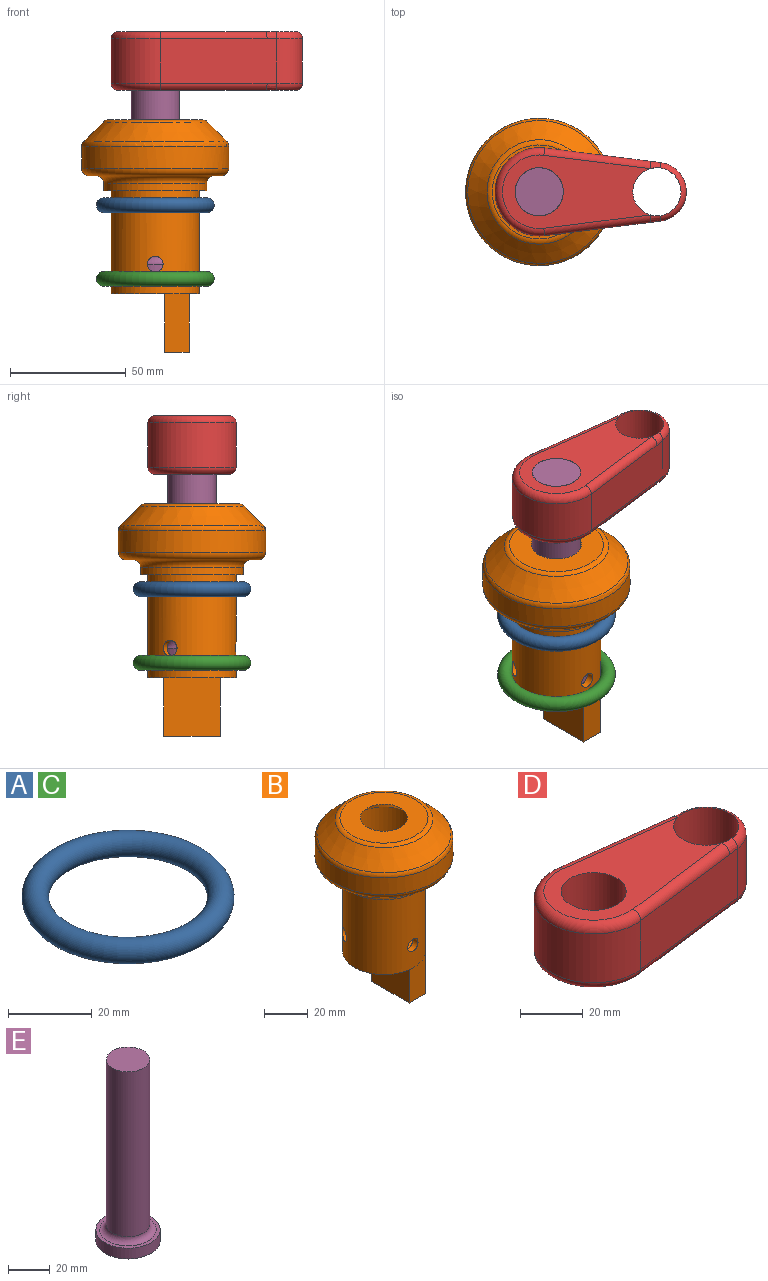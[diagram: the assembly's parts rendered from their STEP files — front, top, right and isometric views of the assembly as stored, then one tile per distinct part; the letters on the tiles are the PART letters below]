
ASSEMBLY  parts=5 mates=4
PART A: 1 faces, bbox 55x55x6.4 mm
  f0: torus R=22.23mm, axis (0,0,1), area 2785.8mm2
PART B: 24 faces, bbox 68.7x68.7x100.3 mm
  f0: plane 38.1x33.64mm, normal (0,0,-1), area 810.7mm2, adj f2,f19,f21,f22
  f1: plane 24.49x4.46mm, normal (0,0,-1), area 74.7mm2, adj f2,f20
  f2: cylinder r=19.05mm len=44.45mm, axis (0,0,-1), area 5212.8mm2, adj f0,f1,f5,f12,f13,f14
  f3: cylinder r=15.88mm len=63.5mm, axis (0,0,-1), area 6226mm2, adj f4,f11,f12,f13,f14
  f4: plane 31.75x31.75mm, normal (0,0,1), area 791.7mm2, adj f3
  f5: plane 44.45x44.45mm, normal (0,0,-1), area 411.7mm2, adj f2,f6
  f6: cylinder r=22.23mm len=44.45mm, axis (0,0,-1), area 443.4mm2, adj f5,f15
  f7: plane 57.15x57.15mm, normal (0,0,-1), area 538.4mm2, adj f15,f16
  f8: cylinder r=31.75mm len=63.5mm, axis (0,0,-1), area 1891.2mm2, adj f16,f17
  f9: cone r=31.75mm half-angle=45deg, axis (0,0,-1), area 1967mm2, adj f17,f18
  f10: plane 40.55x40.55mm, normal (0,0,1), area 925.3mm2, adj f11,f18
  f11: cone r=15.88mm half-angle=45deg, axis (0,0,-1), area 601.9mm2, adj f3,f10
  f12: cylinder r=3.38mm len=6.76mm, axis (0,1,0), area 68mm2, adj f2,f3
  f13: cylinder r=3.38mm len=7.62mm, axis (0.87,-0.5,0), area 68mm2, adj f2,f3
  f14: cylinder r=3.38mm len=7.62mm, axis (-0.87,-0.5,0), area 68mm2, adj f2,f3
  f15: torus R=25.4mm, axis (0,0,-1), area 732.6mm2, adj f6,f7
  f16: torus R=28.57mm, axis (0,0,-1), area 958.8mm2, adj f7,f8
  f17: torus R=28.57mm, axis (0,0,1), area 492.5mm2, adj f8,f9
  f18: torus R=20.27mm, axis (0,0,1), area 336.2mm2, adj f9,f10
  f19: plane 25.4x10.4mm, normal (0,1,0), area 264.1mm2, adj f0,f20,f22,f23
  f20: plane 25.4x24.49mm, normal (1,0,0), area 622.1mm2, adj f1,f19,f21,f23
  f21: plane 25.4x10.4mm, normal (0,-1,0), area 264.1mm2, adj f0,f20,f22,f23
  f22: plane 25.4x24.49mm, normal (-1,0,0), area 622.1mm2, adj f0,f19,f21,f23
  f23: plane 24.49x10.4mm, normal (0,0,-1), area 254.7mm2, adj f19,f20,f21,f22
PART C: same geometry as A
PART D: 20 faces, bbox 85.2x41.2x25.6 mm
  f0: cylinder r=19.05mm len=38.1mm, axis (0,0,1), area 1231.1mm2, adj f1,f4,f8,f16
  f1: plane 50.01x19.3mm, normal (0.12,-0.99,0), area 960.7mm2, adj f0,f2,f9,f11,f14,f15
  f2: cylinder r=12.7mm len=25.2mm, axis (0,0,1), area 708.4mm2, adj f1,f4,f13,f17
  f3: cylinder r=10.4mm len=25.4mm, axis (0,0,1), area 1659.5mm2, adj f5,f6
  f4: plane 50.01x19.3mm, normal (0.12,0.99,0), area 960.7mm2, adj f0,f2,f10,f12,f18,f19
  f5: plane 63.73x31.75mm, normal (0,0,-1), area 1189.5mm2, adj f3,f7,f14,f16,f18
  f6: plane 63.73x31.75mm, normal (0,0,1), area 1189.5mm2, adj f3,f7,f8,f9,f10
  f7: cylinder r=10.4mm len=25.4mm, axis (0,0,1), area 1659.5mm2, adj f5,f6,f11,f12,f13,f15,f17,f19
  f8: torus R=15.88mm, axis (0,0,1), area 302.8mm2, adj f0,f6,f9,f10
  f9: cylinder r=3.17mm len=46.27mm, axis (0.99,0.12,0), area 230.6mm2, adj f1,f6,f8,f11
  f10: cylinder r=3.17mm len=46.27mm, axis (-0.99,0.12,0), area 230.6mm2, adj f4,f6,f8,f12
  f11: bspline ~5.71x3.26mm, area 18.3mm2, adj f1,f7,f9,f13
  f12: bspline ~5.71x3.26mm, area 18.3mm2, adj f4,f7,f10,f13
  f13: torus R=9.53mm, axis (0,0,1), area 141mm2, adj f2,f7,f11,f12
  f14: cylinder r=3.17mm len=46.27mm, axis (-0.99,-0.12,0), area 230.6mm2, adj f1,f5,f15,f16
  f15: bspline ~5.71x3.26mm, area 18.3mm2, adj f1,f7,f14,f17
  f16: torus R=15.88mm, axis (0,0,1), area 302.8mm2, adj f0,f5,f14,f18
  f17: torus R=9.53mm, axis (0,0,-1), area 141mm2, adj f2,f7,f15,f19
  f18: cylinder r=3.17mm len=46.27mm, axis (0.99,-0.12,0), area 230.6mm2, adj f4,f5,f16,f19
  f19: bspline ~5.71x3.26mm, area 18.3mm2, adj f4,f7,f17,f18
PART E: 6 faces, bbox 34.3x34.3x106.7 mm
  f0: plane 30.96x30.96mm, normal (0,0,-1), area 752.6mm2, adj f1
  f1: cylinder r=15.48mm len=30.96mm, axis (0,0,1), area 617.5mm2, adj f0,f2
  f2: plane 30.96x30.96mm, normal (0,0,1), area 173.9mm2, adj f1,f5
  f3: cylinder r=10.4mm len=97.16mm, axis (0,0,1), area 6347.5mm2, adj f4,f5
  f4: plane 20.8x20.8mm, normal (0,0,1), area 339.7mm2, adj f3
  f5: torus R=13.57mm, axis (0,0,1), area 362mm2, adj f2,f3
PLACE A t=(0,0,38.1)mm
PLACE B at identity fixed
PLACE C t=(0,0,6.35)mm
PLACE D rot(axis=(0,0,1),0deg) t=(0,0,0)mm
PLACE E rot(axis=(0,0,-1),90deg) t=(0,0,0)mm
MATE fastened E.f1 <-> D.f0  axis (0,0,1) through (0,0,113.03)mm
MATE fastened A.f0 <-> B.f2  axis (0,0,1) through (0,0,38.1)mm
MATE cylindrical E.f1 <-> B.f2  axis (0,0,-1) through (0,0,6.35)mm
MATE fastened C.f0 <-> B.f2  axis (0,0,1) through (0,0,6.35)mm
